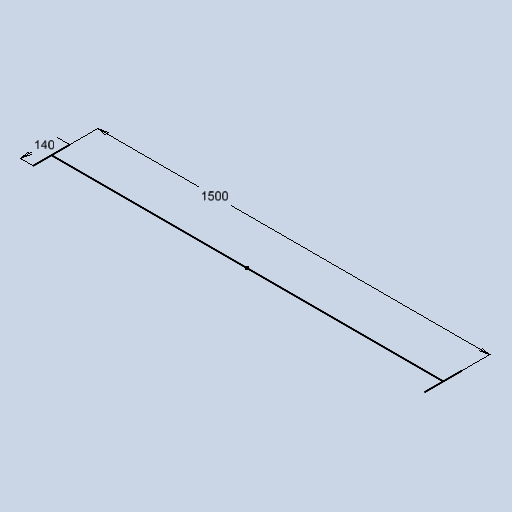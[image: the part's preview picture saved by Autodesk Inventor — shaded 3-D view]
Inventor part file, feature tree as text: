
AUTODESK INVENTOR PART (.ipt)
format: ipt  version: 2025 (Build 290162010, 162A)  size: 126,976 bytes
history: native  units: mm
features: sketch x1
ambient origin geometry x8: Origin, YZ Plane, XZ Plane, XY Plane, X Axis, Y Axis, Z Axis, Center Point
feature tree (1):
  sketch  "Sketch1"  dims[d0=140.0mm d1=1500.0mm]
